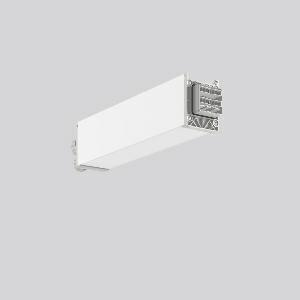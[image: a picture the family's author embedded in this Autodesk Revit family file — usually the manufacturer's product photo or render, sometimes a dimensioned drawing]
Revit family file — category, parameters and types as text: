
# Revit family: linedo_anfangseinspeisung_7pol_s_982678_002_3_a9b5
name_source: partatom
category: Lighting Fixtures
units: mm (PartAtom-declared; Revit-internal decimal feet)

## family parameters
Cut with Voids When Loaded = No
Host = Face
Light Source = No
Part Type = Normal
Room Calculation Point = No
Round Connector Dimension = Use Diameter
Shared = No

## types (1)
- LINEDO_Anfangseinspeisung_7pol_S
    Apparent Load = 0 VA
    Default Elevation = 1800 mm
    Description = Series: LINEDO
Initial power feed, 7-pole, connection plug. Housing: extruded aluminium profile, powder-coated. Cover made of plastic, surface like housing. LINEDO plug system, plastic, light grey. 2 cable glands (M20 and M25). Cable glands on side or on top. Easy connection for rigid or flexible wires.
Colour: white
Length: 330 mm
Width: 58 mm
Height: 76 mm
Weight: 673 g
    Height = 76 mm
    Lamp = 0 x
    Length = 312 mm
    Luminous efficacy = 0 lm/W
    Manufacturer = RZB
    ModVariant = No
    Model = 982678.002.3
    Mounting Place = Ceiling
    Mounting Type = Pendant, Surface mounted
    Number of Poles = 1
    OnlyDefault = Yes
    Power Factor = 1
    Product Name = LINEDO_Anfangseinspeisung_7pol_S
    Product group = Surface mounted continuous line luminaire system
    ProductGroupID = 310
    Protection Class = Protection class I
    Protection Degree = IP 54
    RLX_Detail_Level = 1
    RLX_Emergency_Light_Flux = 0 lm
    RLX_Emergency_Type = 0
    RLX_Emergency_Type_DB = No
    RlxData = <blob elided: 12193 chars, md5=8b44efb1>
    Standby Power = 0 W
    System Light Flux = 0 lm
    System Power = 0 W
    Type Comments = Product without accessories
    Type Image = 982678.002.1.jpg
    URL = http://relux.com
    VarID = ---
    Voltage = 0 V
    Weight = 0.00 kg
    Width = 58 mm

## geometry (parser evidence)
native form markers: Sweep x8
no freeform markers — native parametric forms only
